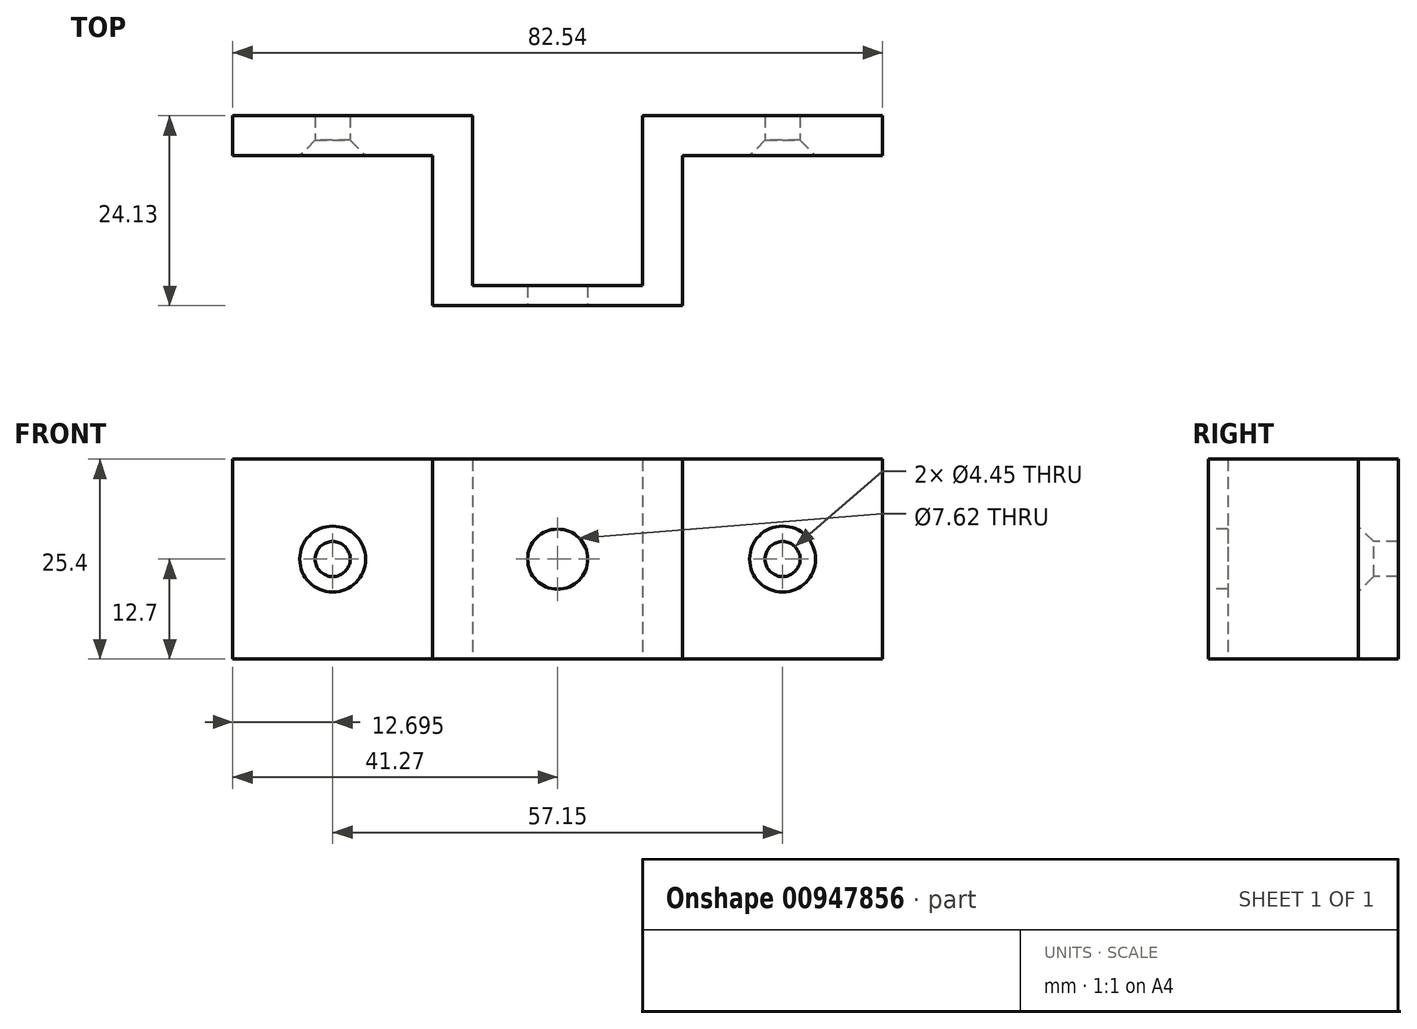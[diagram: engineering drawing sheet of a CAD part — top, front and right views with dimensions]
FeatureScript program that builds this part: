
annotation { "Feature Type Name" : "Feature", "Feature Type Description" : "" }
export const myFeature = defineFeature(function(context is Context, id is Id, definition is map)
    precondition{}
    {
        {
            var Q0;
            Q0=qCreatedBy(makeId("Top.planeOp"),FACE);
            var sketch = newSketch(context, id + "F0", { "sketchPlane" : qUnion([Q0])});
            skLineSegment(sketch, "E0", {"start": v(-41.28, 24.13) * mm, "end": v(-41.28, 19.05) * mm});
            skLineSegment(sketch, "E1", {"start": v(-41.27, 19.05) * mm, "end": v(-15.87, 19.05) * mm});
            skLineSegment(sketch, "E2", {"start": v(-15.87, 19.05) * mm, "end": v(-15.87, 0) * mm});
            skLineSegment(sketch, "E3", {"start": v(-15.87, 0) * mm, "end": v(15.87, 0) * mm});
            skLineSegment(sketch, "E4", {"start": v(15.88, 0) * mm, "end": v(15.87, 19.05) * mm});
            skLineSegment(sketch, "E5", {"start": v(15.88, 19.05) * mm, "end": v(41.28, 19.05) * mm});
            skLineSegment(sketch, "E6", {"start": v(41.28, 19.05) * mm, "end": v(41.28, 24.13) * mm});
            skLineSegment(sketch, "E7", {"start": v(-41.28, 24.13) * mm, "end": v(-10.8, 24.13) * mm});
            skLineSegment(sketch, "E8", {"start": v(-10.8, 24.13) * mm, "end": v(-10.8, 2.54) * mm});
            skLineSegment(sketch, "E9", {"start": v(-10.8, 2.54) * mm, "end": v(10.8, 2.54) * mm});
            skLineSegment(sketch, "E10", {"start": v(10.8, 2.54) * mm, "end": v(10.8, 24.13) * mm});
            skLineSegment(sketch, "E11", {"start": v(10.8, 24.13) * mm, "end": v(41.28, 24.13) * mm});
            skSolve(sketch);
        }
        {
            var Q0;
            Q0 = qSketchRegion(id + "F0", true);
            extrude(context, id + "F1", {"entities" : qUnion([Q0]), "depth" : 25.4 * mm, "offsetDistance" : 25 * mm});
        }
        {
            var Q0;
            Q0=makeQuery(id+"F1.opExtrude","SWEPT_FACE",FACE,{"disambiguationData":[OSD([sQuery(id+"F0.wireOp",EDGE,"E3")])]});
            var sketch = newSketch(context, id + "F2", { "sketchPlane" : qUnion([Q0])});
            skCircle(sketch, "E12", {"center": v(0, 12.7) * mm, "radius": 3.37 * mm});
            skSolve(sketch);
        }
        {
            var Q0;
            Q0=sQuery(id+"F2.wireOp",VERTEX,"E12.center");
            var Q1;
            Q1=makeQuery(id+"F1.opExtrude","SWEPT_BODY",BODY,{"disambiguationData":[OSD([sQuery(id+"F0.wireOp",EDGE,"E0"),sQuery(id+"F0.wireOp",EDGE,"E1"),sQuery(id+"F0.wireOp",EDGE,"E2"),sQuery(id+"F0.wireOp",EDGE,"E3"),sQuery(id+"F0.wireOp",EDGE,"E4"),sQuery(id+"F0.wireOp",EDGE,"E5"),sQuery(id+"F0.wireOp",EDGE,"E6"),sQuery(id+"F0.wireOp",EDGE,"E7"),sQuery(id+"F0.wireOp",EDGE,"E8"),sQuery(id+"F0.wireOp",EDGE,"E9"),sQuery(id+"F0.wireOp",EDGE,"E10"),sQuery(id+"F0.wireOp",EDGE,"E11")])]});
            hole(context, id + "F3", {"style" : HoleStyle.SIMPLE, "endStyle" : HoleEndStyle.THROUGH, "holeDiameter" : 7.62 * mm, "majorDiameter" : 5 * mm, "isTappedThrough" : true, "tappedDepth" : 12 * mm, "tapClearance" : 3, "locations" : qUnion([Q0]), "scope" : qUnion([Q1])});
        }
        {
            var Q0;
            Q0=makeQuery(id+"F1.opExtrude","SWEPT_FACE",FACE,{"disambiguationData":[OSD([sQuery(id+"F0.wireOp",EDGE,"E1")])]});
            var sketch = newSketch(context, id + "F4", { "sketchPlane" : qUnion([Q0])});
            skPoint(sketch, "E13", {"position": v(-28.58, 12.7) * mm});
            skSolve(sketch);
        }
        {
            var Q0;
            Q0=makeQuery(id+"F1.opExtrude","SWEPT_FACE",FACE,{"disambiguationData":[OSD([sQuery(id+"F0.wireOp",EDGE,"E5")])]});
            var sketch = newSketch(context, id + "F5", { "sketchPlane" : qUnion([Q0])});
            skPoint(sketch, "E14", {"position": v(28.58, 12.7) * mm});
            skSolve(sketch);
        }
        {
            var Q0;
            Q0=sQuery(id+"F4.wireOp",VERTEX,"E13");
            var Q1;
            Q1=makeQuery(id+"F1.opExtrude","SWEPT_BODY",BODY,{"disambiguationData":[OSD([sQuery(id+"F0.wireOp",EDGE,"E0"),sQuery(id+"F0.wireOp",EDGE,"E1"),sQuery(id+"F0.wireOp",EDGE,"E2"),sQuery(id+"F0.wireOp",EDGE,"E3"),sQuery(id+"F0.wireOp",EDGE,"E4"),sQuery(id+"F0.wireOp",EDGE,"E5"),sQuery(id+"F0.wireOp",EDGE,"E6"),sQuery(id+"F0.wireOp",EDGE,"E7"),sQuery(id+"F0.wireOp",EDGE,"E8"),sQuery(id+"F0.wireOp",EDGE,"E9"),sQuery(id+"F0.wireOp",EDGE,"E10"),sQuery(id+"F0.wireOp",EDGE,"E11")])]});
            hole(context, id + "F6", {"style" : HoleStyle.C_SINK, "endStyle" : HoleEndStyle.THROUGH, "holeDiameter" : 4.44 * mm, "cSinkDiameter" : 8.38 * mm, "cSinkAngle" : 90 * degree, "majorDiameter" : 5 * mm, "isTappedThrough" : true, "tappedDepth" : 12 * mm, "tapClearance" : 3, "locations" : qUnion([Q0]), "scope" : qUnion([Q1])});
        }
        {
            var Q0;
            Q0=sQuery(id+"F5.wireOp",VERTEX,"E14");
            var Q1;
            Q1=makeQuery(id+"F1.opExtrude","SWEPT_BODY",BODY,{"disambiguationData":[OSD([sQuery(id+"F0.wireOp",EDGE,"E0"),sQuery(id+"F0.wireOp",EDGE,"E1"),sQuery(id+"F0.wireOp",EDGE,"E2"),sQuery(id+"F0.wireOp",EDGE,"E3"),sQuery(id+"F0.wireOp",EDGE,"E4"),sQuery(id+"F0.wireOp",EDGE,"E5"),sQuery(id+"F0.wireOp",EDGE,"E6"),sQuery(id+"F0.wireOp",EDGE,"E7"),sQuery(id+"F0.wireOp",EDGE,"E8"),sQuery(id+"F0.wireOp",EDGE,"E9"),sQuery(id+"F0.wireOp",EDGE,"E10"),sQuery(id+"F0.wireOp",EDGE,"E11")])]});
            hole(context, id + "F7", {"style" : HoleStyle.C_SINK, "endStyle" : HoleEndStyle.THROUGH, "holeDiameter" : 4.44 * mm, "cSinkDiameter" : 8.38 * mm, "cSinkAngle" : 90 * degree, "majorDiameter" : 5 * mm, "isTappedThrough" : true, "tappedDepth" : 12 * mm, "tapClearance" : 3, "locations" : qUnion([Q0]), "scope" : qUnion([Q1])});
        }
    });
